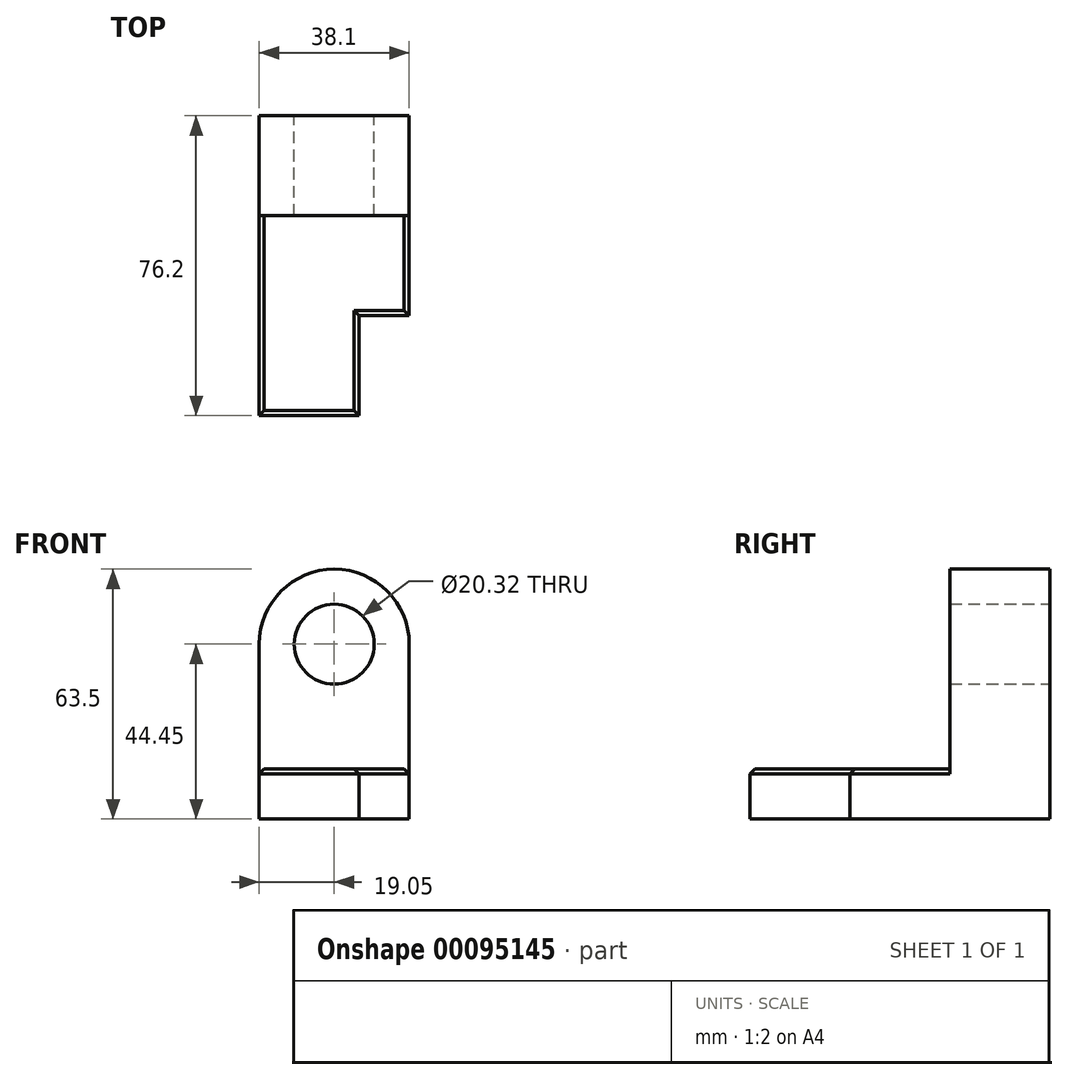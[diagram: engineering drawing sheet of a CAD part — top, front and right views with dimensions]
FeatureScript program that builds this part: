
annotation { "Feature Type Name" : "Feature", "Feature Type Description" : "" }
export const myFeature = defineFeature(function(context is Context, id is Id, definition is map)
    precondition{}
    {
        {
            var Q0;
            Q0=qCreatedBy(makeId("Front.planeOp"),FACE);
            var sketch = newSketch(context, id + "F0", { "sketchPlane" : qUnion([Q0])});
            skLineSegment(sketch, "E0.bottom", {"start": v(-19.05, -31.75) * mm, "end": v(19.05, -31.75) * mm});
            skLineSegment(sketch, "E0.top", {"start": v(-19.05, 31.75) * mm, "end": v(19.05, 31.75) * mm});
            skLineSegment(sketch, "E0.left", {"start": v(-19.05, -31.75) * mm, "end": v(-19.05, 31.75) * mm});
            skLineSegment(sketch, "E0.right", {"start": v(19.05, -31.75) * mm, "end": v(19.05, 31.75) * mm});
            skPoint(sketch, "E0.middle", {"position": v(0, 0) * mm});
            skPoint(sketch, "E1", {"position": v(-19.05, 12.7) * mm});
            skPoint(sketch, "E2", {"position": v(19.05, 12.7) * mm});
            skPoint(sketch, "E3", {"position": v(0, 31.75) * mm});
            skArc(sketch, "E4", {"start": v(19.05, 12.7) * mm, "mid": v(0, 31.75) * mm, "end": v(-19.05, 12.7) * mm});
            skCircle(sketch, "E5", {"center": v(0, 12.7) * mm, "radius": 10.16 * mm});
            skSolve(sketch);
        }
        {
            var Q0;
            {var subQ4=sQuery(id+"F0.wireOp",EDGE,"E0.bottom");Q0=makeQuery(id+"F0.imprint","IMPRINT",FACE,{"disambiguationData":[TD([[makeQuery(id+"F0.imprint","IMPRINT",EDGE,{"derivedFrom":subQ4}),1.0]])]});}
            extrude(context, id + "F1", {"entities" : qUnion([Q0]), "depth" : 25.4 * mm});
        }
        {
            var Q0;
            Q0=makeQuery(id+"F1.opExtrude","CAP_FACE",FACE,{"disambiguationData":[OSD([sQuery(id+"F0.wireOp",EDGE,"E0.bottom"),sQuery(id+"F0.wireOp",EDGE,"E0.left"),sQuery(id+"F0.wireOp",EDGE,"E0.right"),sQuery(id+"F0.wireOp",EDGE,"E4"),sQuery(id+"F0.wireOp",EDGE,"E5")])],"isStart":false});
            var sketch = newSketch(context, id + "F2", { "sketchPlane" : qUnion([Q0])});
            skPoint(sketch, "E6", {"position": v(0, -19.05) * mm});
            skLineSegment(sketch, "E7.bottom", {"start": v(-19.05, -19.05) * mm, "end": v(6.35, -19.05) * mm});
            skLineSegment(sketch, "E7.top", {"start": v(-19.05, -31.75) * mm, "end": v(6.35, -31.75) * mm});
            skLineSegment(sketch, "E7.left", {"start": v(-19.05, -19.05) * mm, "end": v(-19.05, -31.75) * mm});
            skLineSegment(sketch, "E7.right", {"start": v(6.35, -19.05) * mm, "end": v(6.35, -31.75) * mm});
            skSolve(sketch);
        }
        {
            var Q0;
            Q0 = qSketchRegion(id + "F2", true);
            extrude(context, id + "F3", {"entities" : qUnion([Q0]), "operationType" : NewBodyOperationType.ADD, "depth" : 50.8 * mm});
        }
        {
            var Q0;
            Q0=makeQuery(id+"F1.opExtrude","CAP_FACE",FACE,{"disambiguationData":[OSD([sQuery(id+"F0.wireOp",EDGE,"E0.bottom"),sQuery(id+"F0.wireOp",EDGE,"E0.left"),sQuery(id+"F0.wireOp",EDGE,"E0.right"),sQuery(id+"F0.wireOp",EDGE,"E4"),sQuery(id+"F0.wireOp",EDGE,"E5")])],"isStart":false});
            var sketch = newSketch(context, id + "F4", { "sketchPlane" : qUnion([Q0])});
            skLineSegment(sketch, "E8.bottom", {"start": v(6.35, -19.05) * mm, "end": v(19.05, -19.05) * mm});
            skLineSegment(sketch, "E8.top", {"start": v(6.35, -31.75) * mm, "end": v(19.05, -31.75) * mm});
            skLineSegment(sketch, "E8.left", {"start": v(6.35, -19.05) * mm, "end": v(6.35, -31.75) * mm});
            skLineSegment(sketch, "E8.right", {"start": v(19.05, -19.05) * mm, "end": v(19.05, -31.75) * mm});
            skSolve(sketch);
        }
        {
            var Q0;
            Q0=makeQuery(id+"F4.imprint","IMPRINT",FACE,{"disambiguationData":[TD([[makeQuery(id+"F4.imprint","IMPRINT",EDGE,{"derivedFrom":sQuery(id+"F4.wireOp",EDGE,"E8.bottom")}),-1.0]])]});
            extrude(context, id + "F5", {"entities" : qUnion([Q0]), "operationType" : NewBodyOperationType.ADD, "depth" : 25.4 * mm});
        }
        {
            var Q0;
            Q0=makeQuery(id+"F3.opExtrude","SWEPT_EDGE",EDGE,{"disambiguationData":[OSD([sQuery(id+"F0.wireOp",EDGE,"E0.left"),sQuery(id+"F2.wireOp",EDGE,"E7.bottom"),sQuery(id+"F2.wireOp",EDGE,"E7.left")])]});
            var Q1;
            Q1=makeQuery(id+"F3.opExtrude","CAP_EDGE",EDGE,{"disambiguationData":[OSD([sQuery(id+"F2.wireOp",EDGE,"E7.bottom")])],"isStart":false});
            var Q2;
            Q2=makeQuery(id+"F3.opExtrude","SWEPT_EDGE",EDGE,{"disambiguationData":[OSD([sQuery(id+"F2.wireOp",EDGE,"E7.bottom"),sQuery(id+"F2.wireOp",EDGE,"E7.right")])]});
            var Q3;
            Q3=makeQuery(id+"F5.opExtrude","CAP_EDGE",EDGE,{"disambiguationData":[OSD([sQuery(id+"F4.wireOp",EDGE,"E8.bottom")])],"isStart":false});
            var Q4;
            Q4=makeQuery(id+"F5.opExtrude","SWEPT_EDGE",EDGE,{"disambiguationData":[OSD([sQuery(id+"F0.wireOp",EDGE,"E0.right"),sQuery(id+"F4.wireOp",EDGE,"E8.bottom"),sQuery(id+"F4.wireOp",EDGE,"E8.right")])]});
            chamfer(context, id + "F6", {"entities" : qUnion([Q0, Q1, Q2, Q3, Q4]), "width" : 1.27 * mm, "tangentPropagation" : true});
        }
    });
